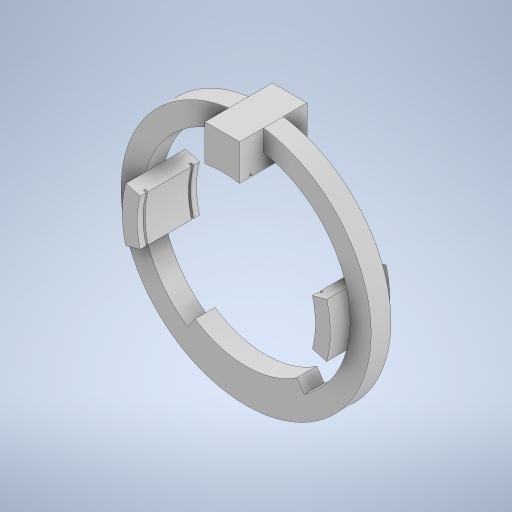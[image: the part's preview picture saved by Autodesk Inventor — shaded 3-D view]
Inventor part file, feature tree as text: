
AUTODESK INVENTOR PART (.ipt)
format: ipt  version: 2024 (Build 280153000, 153)  size: 421,376 bytes
history: native  units: in
note: dims shown in document units (in); Inventor stores cm internally (conversion verified against a paired STEP export)
features: extrude x10, sketch x10, plane x4, mirror x4
ambient origin geometry x8: Origin, YZ Plane, XZ Plane, XY Plane, X Axis, Y Axis, Z Axis, Center Point
bodies: Solid1 (feature_tree)
feature tree (28):
  extrude  "Extrusion1"  Depth=0.5906in
  extrude  "Extrusion2"  Depth=1.9685in TaperAngle=0.0deg
  extrude  "Extrusion3"  Depth=4.3307in
  plane  "Work Plane1"
  mirror  "Mirror1"
  plane  "Work Plane2"
  extrude  "Extrusion4"  Depth=0.3937in TaperAngle=0.0deg
  extrude  "Extrusion5"  Depth=4.3307in
  mirror  "Mirror2"
  plane  "Work Plane4"
  extrude  "Extrusion6"  Depth=3.937in TaperAngle=0.0deg
  extrude  "Extrusion7"  Depth=0.2336in
  extrude  "Extrusion8"  Depth=17.7165in
  extrude  "Extrusion9"  TaperAngle=15.0deg  [1 undecoded]
  extrude  "Extrusion10"  Depth=17.7165in
  mirror  "Mirror3"
  mirror  "Mirror4"
  sketch  "Sketch1"  dims[d4=8.6614in d5=0.0in d7=0.5906in]
  sketch  "Sketch2"  dims[d8=0.3937in d9=0.0in d10=1.9685in d11=0.0in]
  sketch  "Sketch3"  dims[d12=18.3071in d13=4.3307in]
  sketch  "Sketch4"  dims[d14=-0.7874in d15=0.3937in d16=0.0in]
  sketch  "Sketch5"  dims[d17=0.3937in d18=0.0in d19=4.3307in]
  plane  "Work Plane3"
  sketch  "Sketch7"  dims[d20=41.3386in d21=3.937in d22=0.0in]
  sketch  "Sketch8"  dims[d24=0.2336in d25=0.2336in]
  sketch  "Sketch9"  dims[d26=3.937in d27=0.0in d28=17.7165in]
  sketch  "Sketch10"  dims[d29=18.1102in d30=15.0deg]
  sketch  "Sketch11"  dims[d31=30.0deg d32=17.7165in d33=15.0deg d34=30.0deg d35=8.6614in d36=0.0in d37=18.3071in d38=0.3937in d39=0.0in d40=1.1811in d41=0.0in]
note: 1 required parameter value undecoded (feature->parameter linkage not recoverable at this tier; creation-order binding heuristic only, values carry confidence <= 0.55)
